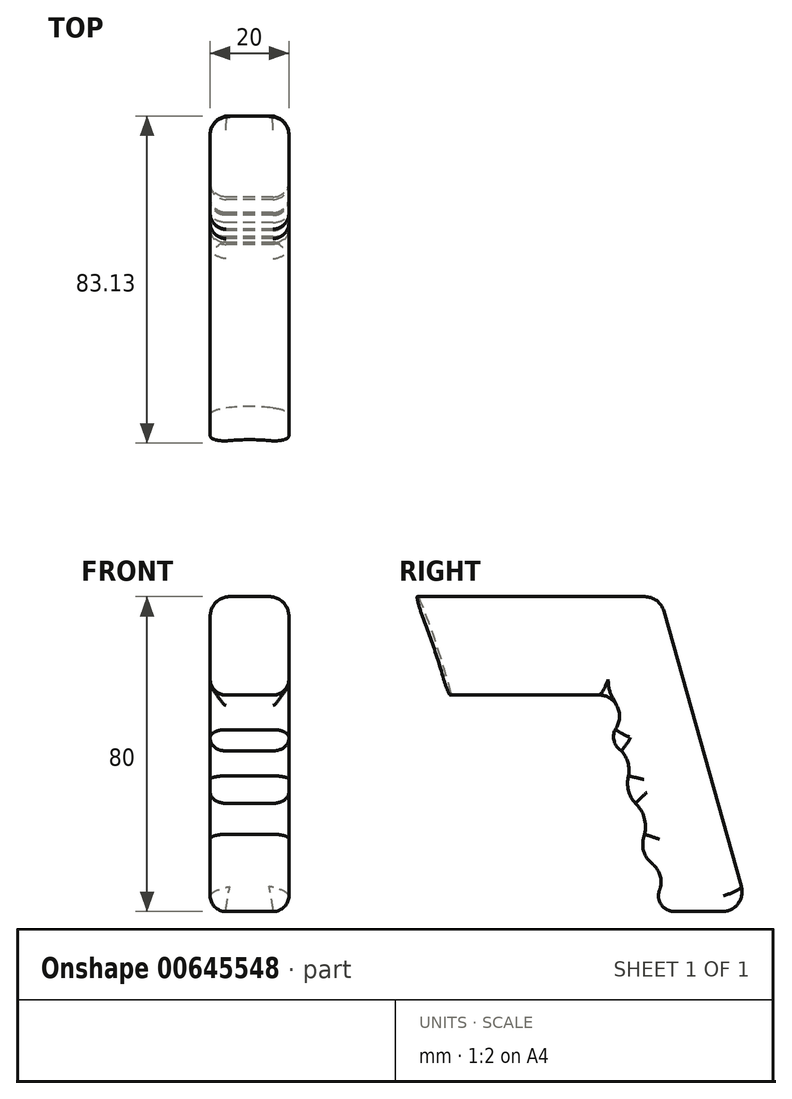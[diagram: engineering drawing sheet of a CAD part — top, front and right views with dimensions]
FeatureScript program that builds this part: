
annotation { "Feature Type Name" : "Feature", "Feature Type Description" : "" }
export const myFeature = defineFeature(function(context is Context, id is Id, definition is map)
    precondition{}
    {
        {
            var Q0;
            Q0=qCreatedBy(makeId("Right.planeOp"),FACE);
            var sketch = newSketch(context, id + "F0", { "sketchPlane" : qUnion([Q0])});
            skLineSegment(sketch, "E0", {"start": v(0, 0) * mm, "end": v(75, 0) * mm});
            skLineSegment(sketch, "E1", {"start": v(0, 0) * mm, "end": v(0, 200) * mm});
            skFitSpline(sketch, "E2", {"points": [v(0, 200) * mm, v(75, 0) * mm], "startDerivative": vector(195.84, 0) * mm, "endDerivative": vector(0, -233.52) * mm});
            skLineSegment(sketch, "E3", {"start": v(0, 200) * mm, "end": v(-73.01, 200) * mm, "construction": true});
            skLineSegment(sketch, "E4", {"start": v(75, 0) * mm, "end": v(75, -62.44) * mm, "construction": true});
            skSolve(sketch);
        }
        {
            var Q0;
            Q0=qCreatedBy(makeId("Right.planeOp"),FACE);
            var sketch = newSketch(context, id + "F1", { "sketchPlane" : qUnion([Q0])});
            skLineSegment(sketch, "E5", {"start": v(0, 0) * mm, "end": v(0, 155) * mm});
            skSolve(sketch);
        }
        {
            var Q0;
            Q0=qCreatedBy(makeId("Right.planeOp"),FACE);
            var sketch = newSketch(context, id + "F2", { "sketchPlane" : qUnion([Q0])});
            skLineSegment(sketch, "E6", {"start": v(0, 155) * mm, "end": v(114.73, 155) * mm});
            skLineSegment(sketch, "E7", {"start": v(114.73, 155) * mm, "end": v(137.23, 75) * mm});
            skLineSegment(sketch, "E8", {"start": v(137.23, 75) * mm, "end": v(116.25, 75) * mm});
            skLineSegment(sketch, "E9", {"start": v(100.9, 130) * mm, "end": v(0, 130) * mm});
            skLineSegment(sketch, "E10", {"start": v(0, 130) * mm, "end": v(0, 155) * mm});
            skArc(sketch, "E11", {"start": v(103.42, 121.2) * mm, "mid": v(104.26, 126.2) * mm, "end": v(100.9, 130) * mm});
            skArc(sketch, "E12", {"start": v(103.42, 121.2) * mm, "mid": v(103.15, 118.21) * mm, "end": v(104.96, 115.82) * mm});
            skArc(sketch, "E13", {"start": v(106.78, 109.46) * mm, "mid": v(106.61, 112.86) * mm, "end": v(104.96, 115.82) * mm});
            skArc(sketch, "E14", {"start": v(106.78, 109.46) * mm, "mid": v(106.75, 105.75) * mm, "end": v(108.57, 102.5) * mm});
            skArc(sketch, "E15", {"start": v(110.83, 94.63) * mm, "mid": v(110.76, 98.87) * mm, "end": v(108.57, 102.5) * mm});
            skArc(sketch, "E16", {"start": v(110.83, 94.63) * mm, "mid": v(110.65, 90.38) * mm, "end": v(113.05, 86.88) * mm});
            skArc(sketch, "E17", {"start": v(114.8, 80.78) * mm, "mid": v(114.84, 84.1) * mm, "end": v(113.05, 86.88) * mm});
            skArc(sketch, "E18", {"start": v(114.8, 80.78) * mm, "mid": v(114.52, 77.64) * mm, "end": v(116.25, 75) * mm});
            skSolve(sketch);
        }
        {
            var Q0;
            Q0 = qSketchRegion(id + "F2", true);
            extrude(context, id + "F3", {"entities" : qUnion([Q0]), "endBound" : BoundingType.SYMMETRIC, "depth" : 20 * mm, "offsetDistance" : 25 * mm});
        }
        {
            var Q0;
            Q0=makeQuery(id+"F0.imprint","IMPRINT",FACE,{"disambiguationData":[TD([[makeQuery(id+"F0.imprint","IMPRINT",EDGE,{"derivedFrom":sQuery(id+"F0.wireOp",EDGE,"E0")}),1.0]])]});
            var Q1;
            Q1=sQuery(id+"F1.wireOp",EDGE,"E5");
            revolve(context, id + "F4", {"operationType" : NewBodyOperationType.REMOVE, "entities" : qUnion([Q0]), "axis" : qUnion([Q1]), "revolveType" : RevolveType.FULL, "oppositeDirection" : true});
        }
        {
            var Q0;
            Q0=makeQuery(id+"F3.opExtrude","CAP_EDGE",EDGE,{"disambiguationData":[OSD([sQuery(id+"F2.wireOp",EDGE,"E6")])],"isStart":false});
            var Q1;
            Q1=makeQuery(id+"F3.opExtrude","CAP_EDGE",EDGE,{"disambiguationData":[OSD([sQuery(id+"F2.wireOp",EDGE,"E6")])],"isStart":true});
            var Q2;
            Q2=makeQuery(id+"F3.opExtrude","SWEPT_FACE",FACE,{"disambiguationData":[OSD([sQuery(id+"F2.wireOp",EDGE,"E7")])]});
            fillet(context, id + "F5", {"entities" : qUnion([Q0, Q1, Q2]), "radius" : 5 * mm, "tangentPropagation" : true, "allowEdgeOverflow" : false});
        }
        {
            var Q0;
            Q0=makeQuery(id+"F3.opExtrude","CAP_EDGE",EDGE,{"disambiguationData":[OSD([sQuery(id+"F2.wireOp",EDGE,"E9")])],"isStart":false});
            var Q1;
            Q1=makeQuery(id+"F3.opExtrude","CAP_EDGE",EDGE,{"disambiguationData":[OSD([sQuery(id+"F2.wireOp",EDGE,"E9")])],"isStart":true});
            var Q2;
            Q2=makeQuery(id+"F3.opExtrude","CAP_EDGE",EDGE,{"disambiguationData":[OSD([sQuery(id+"F2.wireOp",EDGE,"E11")])],"isStart":false});
            var Q3;
            Q3=makeQuery(id+"F3.opExtrude","CAP_EDGE",EDGE,{"disambiguationData":[OSD([sQuery(id+"F2.wireOp",EDGE,"E11")])],"isStart":true});
            var Q4;
            Q4=makeQuery(id+"F3.opExtrude","CAP_EDGE",EDGE,{"disambiguationData":[OSD([sQuery(id+"F2.wireOp",EDGE,"E12")])],"isStart":true});
            var Q5;
            Q5=makeQuery(id+"F3.opExtrude","CAP_EDGE",EDGE,{"disambiguationData":[OSD([sQuery(id+"F2.wireOp",EDGE,"E13")])],"isStart":false});
            var Q6;
            Q6=makeQuery(id+"F3.opExtrude","CAP_EDGE",EDGE,{"disambiguationData":[OSD([sQuery(id+"F2.wireOp",EDGE,"E12")])],"isStart":false});
            var Q7;
            Q7=makeQuery(id+"F3.opExtrude","CAP_EDGE",EDGE,{"disambiguationData":[OSD([sQuery(id+"F2.wireOp",EDGE,"E13")])],"isStart":true});
            var Q8;
            Q8=makeQuery(id+"F3.opExtrude","CAP_EDGE",EDGE,{"disambiguationData":[OSD([sQuery(id+"F2.wireOp",EDGE,"E15")])],"isStart":false});
            var Q9;
            Q9=makeQuery(id+"F3.opExtrude","CAP_EDGE",EDGE,{"disambiguationData":[OSD([sQuery(id+"F2.wireOp",EDGE,"E16")])],"isStart":false});
            var Q10;
            Q10=makeQuery(id+"F3.opExtrude","CAP_EDGE",EDGE,{"disambiguationData":[OSD([sQuery(id+"F2.wireOp",EDGE,"E17")])],"isStart":false});
            var Q11;
            Q11=makeQuery(id+"F3.opExtrude","CAP_EDGE",EDGE,{"disambiguationData":[OSD([sQuery(id+"F2.wireOp",EDGE,"E18")])],"isStart":false});
            var Q12;
            Q12=makeQuery(id+"F3.opExtrude","SWEPT_FACE",FACE,{"disambiguationData":[OSD([sQuery(id+"F2.wireOp",EDGE,"E18")])]});
            var Q13;
            Q13=makeQuery(id+"F3.opExtrude","SWEPT_FACE",FACE,{"disambiguationData":[OSD([sQuery(id+"F2.wireOp",EDGE,"E17")])]});
            var Q14;
            Q14=makeQuery(id+"F3.opExtrude","CAP_EDGE",EDGE,{"disambiguationData":[OSD([sQuery(id+"F2.wireOp",EDGE,"E16")])],"isStart":true});
            var Q15;
            Q15=makeQuery(id+"F3.opExtrude","CAP_EDGE",EDGE,{"disambiguationData":[OSD([sQuery(id+"F2.wireOp",EDGE,"E15")])],"isStart":true});
            var Q16;
            Q16=makeQuery(id+"F3.opExtrude","CAP_EDGE",EDGE,{"disambiguationData":[OSD([sQuery(id+"F2.wireOp",EDGE,"E14")])],"isStart":true});
            var Q17;
            Q17=makeQuery(id+"F3.opExtrude","CAP_EDGE",EDGE,{"disambiguationData":[OSD([sQuery(id+"F2.wireOp",EDGE,"E14")])],"isStart":false});
            var Q18;
            Q18=makeQuery(id+"F3.opExtrude","CAP_EDGE",EDGE,{"disambiguationData":[OSD([sQuery(id+"F2.wireOp",EDGE,"E8")])],"isStart":false});
            var Q19;
            Q19=makeQuery(id+"F3.opExtrude","CAP_EDGE",EDGE,{"disambiguationData":[OSD([sQuery(id+"F2.wireOp",EDGE,"E8")])],"isStart":true});
            fillet(context, id + "F6", {"entities" : qUnion([Q0, Q1, Q2, Q3, Q4, Q5, Q6, Q7, Q8, Q9, Q10, Q11, Q12, Q13, Q14, Q15, Q16, Q17, Q18, Q19]), "radius" : 4 * mm, "tangentPropagation" : true, "allowEdgeOverflow" : false});
        }
        {
            var Q0;
            Q0=makeQuery(id+"F3.opExtrude","SWEPT_EDGE",EDGE,{"disambiguationData":[OSD([sQuery(id+"F2.wireOp",EDGE,"E9"),sQuery(id+"F2.wireOp",EDGE,"E11")])]});
            fillet(context, id + "F7", {"entities" : qUnion([Q0]), "radius" : 5 * mm, "tangentPropagation" : true, "allowEdgeOverflow" : false});
        }
    });
